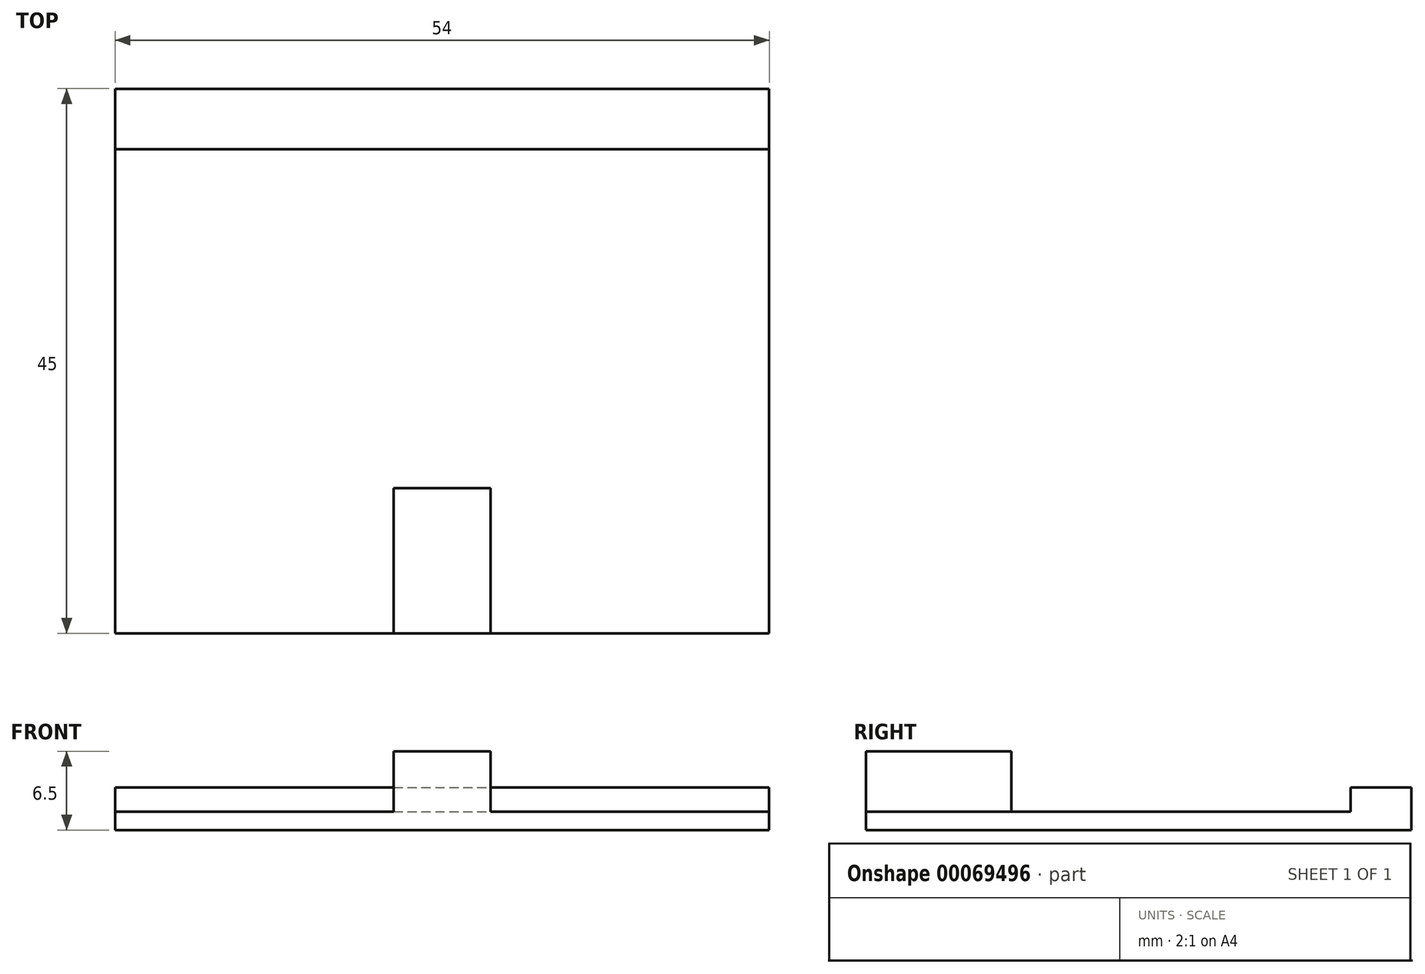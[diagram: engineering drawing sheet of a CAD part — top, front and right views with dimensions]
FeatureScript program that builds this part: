
annotation { "Feature Type Name" : "Feature", "Feature Type Description" : "" }
export const myFeature = defineFeature(function(context is Context, id is Id, definition is map)
    precondition{}
    {
        {
            var Q0;
            Q0=qCreatedBy(makeId("Top.planeOp"),FACE);
            var sketch = newSketch(context, id + "F0", { "sketchPlane" : qUnion([Q0])});
            skLineSegment(sketch, "E0.bottom", {"start": v(-22.54, 25.7) * mm, "end": v(31.46, 25.7) * mm});
            skLineSegment(sketch, "E0.top", {"start": v(-22.54, -19.3) * mm, "end": v(31.46, -19.3) * mm});
            skLineSegment(sketch, "E0.left", {"start": v(-22.54, 25.7) * mm, "end": v(-22.54, -19.3) * mm});
            skLineSegment(sketch, "E0.right", {"start": v(31.46, 25.7) * mm, "end": v(31.46, -19.3) * mm});
            skSolve(sketch);
        }
        {
            var Q0;
            Q0=makeQuery(id+"F0.imprint","IMPRINT",FACE,{"disambiguationData":[TD([[makeQuery(id+"F0.imprint","IMPRINT",EDGE,{"derivedFrom":sQuery(id+"F0.wireOp",EDGE,"E0.bottom")}),-1.0]])]});
            extrude(context, id + "F1", {"entities" : qUnion([Q0]), "depth" : 1.5 * mm});
        }
        {
            var Q0;
            Q0=makeQuery(id+"F1.opExtrude","CAP_FACE",FACE,{"disambiguationData":[OSD([sQuery(id+"F0.wireOp",EDGE,"E0.bottom"),sQuery(id+"F0.wireOp",EDGE,"E0.top"),sQuery(id+"F0.wireOp",EDGE,"E0.left"),sQuery(id+"F0.wireOp",EDGE,"E0.right")])],"isStart":false});
            var sketch = newSketch(context, id + "F2", { "sketchPlane" : qUnion([Q0])});
            skLineSegment(sketch, "E1.bottom", {"start": v(-22.54, 20.7) * mm, "end": v(31.46, 20.7) * mm});
            skLineSegment(sketch, "E1.top", {"start": v(-22.54, 25.7) * mm, "end": v(31.46, 25.7) * mm});
            skLineSegment(sketch, "E1.left", {"start": v(-22.54, 20.7) * mm, "end": v(-22.54, 25.7) * mm});
            skLineSegment(sketch, "E1.right", {"start": v(31.46, 20.7) * mm, "end": v(31.46, 25.7) * mm});
            skSolve(sketch);
        }
        {
            var Q0;
            Q0 = qSketchRegion(id + "F2", true);
            extrude(context, id + "F3", {"entities" : qUnion([Q0]), "operationType" : NewBodyOperationType.ADD, "depth" : 2 * mm});
        }
        {
            var Q0;
            Q0=makeQuery(id+"F1.opExtrude","CAP_FACE",FACE,{"disambiguationData":[OSD([sQuery(id+"F0.wireOp",EDGE,"E0.bottom"),sQuery(id+"F0.wireOp",EDGE,"E0.top"),sQuery(id+"F0.wireOp",EDGE,"E0.left"),sQuery(id+"F0.wireOp",EDGE,"E0.right")])],"isStart":false});
            var sketch = newSketch(context, id + "F4", { "sketchPlane" : qUnion([Q0])});
            skLineSegment(sketch, "E2.bottom", {"start": v(0.46, -19.3) * mm, "end": v(8.46, -19.3) * mm});
            skLineSegment(sketch, "E2.top", {"start": v(0.46, -7.3) * mm, "end": v(8.46, -7.3) * mm});
            skLineSegment(sketch, "E2.left", {"start": v(0.46, -19.3) * mm, "end": v(0.46, -7.3) * mm});
            skLineSegment(sketch, "E2.right", {"start": v(8.46, -19.3) * mm, "end": v(8.46, -7.3) * mm});
            skLineSegment(sketch, "E3", {"start": v(8.46, -7.3) * mm, "end": v(31.46, -7.3) * mm});
            skLineSegment(sketch, "E4", {"start": v(0.46, -7.3) * mm, "end": v(-22.54, -7.3) * mm});
            skSolve(sketch);
        }
        {
            var Q0;
            Q0 = qSketchRegion(id + "F4", true);
            extrude(context, id + "F5", {"entities" : qUnion([Q0]), "operationType" : NewBodyOperationType.ADD, "depth" : 5 * mm});
        }
    });
